# Revit family: Domotics-DomesticRanges-GEWISS-CHORUS_CLIMATE-DAILY-WEEKLY_THERMOSTAT_2M
name_source: partatom
category: Apparecchi elettrici
revit_build: Autodesk Revit 2016 (Build: 20161004_0715(x64)
units: mm (PartAtom-declared; Revit-internal decimal feet)

## family parameters
Condiviso = Sì
Host = Superficie
Mantenere orientamento annotazione = Sì
Numero OmniClass = 23.80.50.11.14
Punto di calcolo locali = Sì
Quota connettore circolare = Usa diametro
Taglio con vuoti quando caricato = Sì
Tipo di parte = Normale
Titolo OmniClass = Switches

## types (3) — shared parameters
Carico apparente = 0 VA
Catalogue = DOMOTICS
Catalogue Range = CHORUS - DOMESTIC RANGE
Description. = Timed thermostat
Electrocod = 1734
IDF = c255b0dc-dd71-4fea-81eb-e24d2b6f70c3
IDT = bb8fe25b-beb4-429f-a986-d7ab8cd39401
Immagine tipo = GW14703.jpg
Larghezza termostato = 46 mm  [stored 0.150919 ft]
N. poli = 2
No. Chorus modules = 2
No. Chorus modules: = 2
Produttore = GEWISS S.p.A.
Prospetto di default = 1219 mm
SEO = Timed thermostat
Simbolo = SIMBOLO CRONOTERMOSTATO SYSTEM : CRONOTERMOSTATO
Supply voltage = 230 V ac - 50/60 Hz
Technical sheet = https://www.gewiss.com
Temperature adjustment = From +5°C to +40°C
Tipo_ = SYSTEM CRONOTERMOSTATI 2M_BASE : TITANIO
URL = https://www.gewiss.com
Version file RFA = 19.0
Volt = 230 V

## per-type parameters (varying)
| type | Colour | Descrizione | EAN code | Modello |
| GW10703 - Timed thermostat fl-mounting 2M 230V white | White | TIMED THERMOSTAT FL-MOUNTING 2M 230VAC W | 8011564261761 | GW10703 |
| GW14703 - Timed thermostat fl-mounting 2M 230V titanium | Titanium | TIMED THERMOSTAT FL-MOUNTING 2M 230VAC T | 8011564268685 | GW14703 |
| GW12703 - Timed thermostat fl-mounting 2M 230V black | Black | TIMED THERMOSTAT FL-MOUNTING 2M 230VAC B | 8011564267459 | GW12703 |

note: [stored X ft] marks values corroborated as IEEE doubles in the binary element streams (Revit-internal decimal feet)

## geometry (parser evidence)
native form markers: Sweep x2
no freeform markers — native parametric forms only
